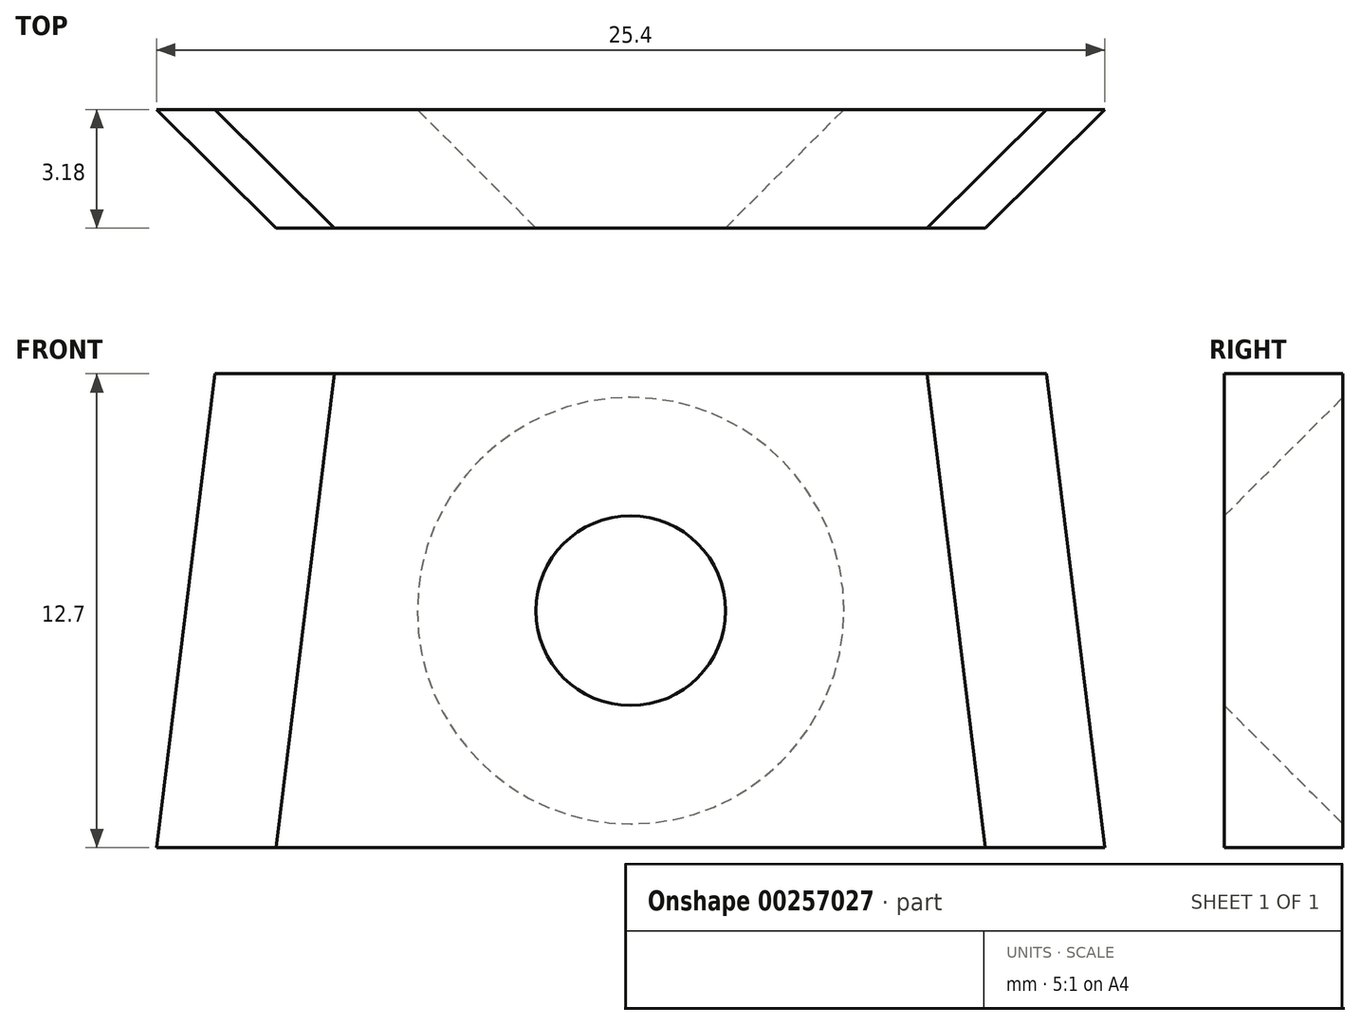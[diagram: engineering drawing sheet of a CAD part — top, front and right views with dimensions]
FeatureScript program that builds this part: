
annotation { "Feature Type Name" : "Feature", "Feature Type Description" : "" }
export const myFeature = defineFeature(function(context is Context, id is Id, definition is map)
    precondition{}
    {
        {
            var Q0;
            Q0=qCreatedBy(makeId("Front.planeOp"),FACE);
            var sketch = newSketch(context, id + "F0", { "sketchPlane" : qUnion([Q0])});
            skLineSegment(sketch, "E0.bottom", {"start": v(0, 0) * mm, "end": v(25.4, 0) * mm});
            skLineSegment(sketch, "E0.top", {"start": v(1.56, 12.7) * mm, "end": v(23.84, 12.7) * mm});
            skLineSegment(sketch, "E1", {"start": v(0, 0) * mm, "end": v(1.56, 12.7) * mm});
            skLineSegment(sketch, "E2", {"start": v(25.4, 0) * mm, "end": v(23.84, 12.7) * mm});
            skLineSegment(sketch, "E3", {"start": v(12.7, 0) * mm, "end": v(12.7, 12.7) * mm, "construction": true});
            skLineSegment(sketch, "E4", {"start": v(0, 0) * mm, "end": v(0, 12.52) * mm, "construction": true});
            skSolve(sketch);
        }
        {
            var Q0;
            Q0=makeQuery(id+"F0.imprint","IMPRINT",FACE,{"disambiguationData":[TD([[makeQuery(id+"F0.imprint","IMPRINT",EDGE,{"derivedFrom":sQuery(id+"F0.wireOp",EDGE,"E0.bottom")}),1.0]])]});
            extrude(context, id + "F1", {"entities" : qUnion([Q0]), "depth" : 3.17 * mm});
        }
        {
            var Q0;
            Q0=makeQuery(id+"F1.opExtrude","CAP_EDGE",EDGE,{"disambiguationData":[OSD([sQuery(id+"F0.wireOp",EDGE,"E2")])],"isStart":false});
            var Q1;
            Q1=makeQuery(id+"F1.opExtrude","CAP_EDGE",EDGE,{"disambiguationData":[OSD([sQuery(id+"F0.wireOp",EDGE,"E1")])],"isStart":false});
            chamfer(context, id + "F2", {"entities" : qUnion([Q0, Q1]), "width" : 3.17 * mm, "tangentPropagation" : true});
        }
        {
            var Q0;
            Q0=makeQuery(id+"F1.opExtrude","CAP_FACE",FACE,{"disambiguationData":[OSD([sQuery(id+"F0.wireOp",EDGE,"E0.bottom"),sQuery(id+"F0.wireOp",EDGE,"E0.top"),sQuery(id+"F0.wireOp",EDGE,"E1"),sQuery(id+"F0.wireOp",EDGE,"E2")])],"isStart":false});
            var sketch = newSketch(context, id + "F3", { "sketchPlane" : qUnion([Q0])});
            skCircle(sketch, "E5", {"center": v(12.7, 6.35) * mm, "radius": 2.54 * mm});
            skLineSegment(sketch, "E6", {"start": v(12.7, 12.7) * mm, "end": v(12.7, 0) * mm, "construction": true});
            skSolve(sketch);
        }
        {
            var Q0;
            Q0=makeQuery(id+"F3.imprint","IMPRINT",FACE,{"disambiguationData":[TD([[makeQuery(id+"F3.imprint","IMPRINT",EDGE,{"derivedFrom":sQuery(id+"F3.wireOp",EDGE,"E5")}),1.0]])]});
            extrude(context, id + "F4", {"entities" : qUnion([Q0]), "operationType" : NewBodyOperationType.REMOVE, "oppositeDirection" : true, "depth" : 25.4 * mm});
        }
        {
            var Q0;
            Q0=makeQuery(id+"F4.boolean.opBoolean","INTERSECT",EDGE,{"derivedFrom":[makeQuery(id+"F1.opExtrude","CAP_FACE",FACE,{"disambiguationData":[OSD([sQuery(id+"F0.wireOp",EDGE,"E0.bottom"),sQuery(id+"F0.wireOp",EDGE,"E0.top"),sQuery(id+"F0.wireOp",EDGE,"E1"),sQuery(id+"F0.wireOp",EDGE,"E2")])],"isStart":true}),makeQuery(id+"F4.opExtrude","SWEPT_FACE",FACE,{"disambiguationData":[OSD([sQuery(id+"F3.wireOp",EDGE,"E5")])]})]});
            chamfer(context, id + "F5", {"entities" : qUnion([Q0]), "width" : 3.17 * mm, "tangentPropagation" : true});
        }
    });
